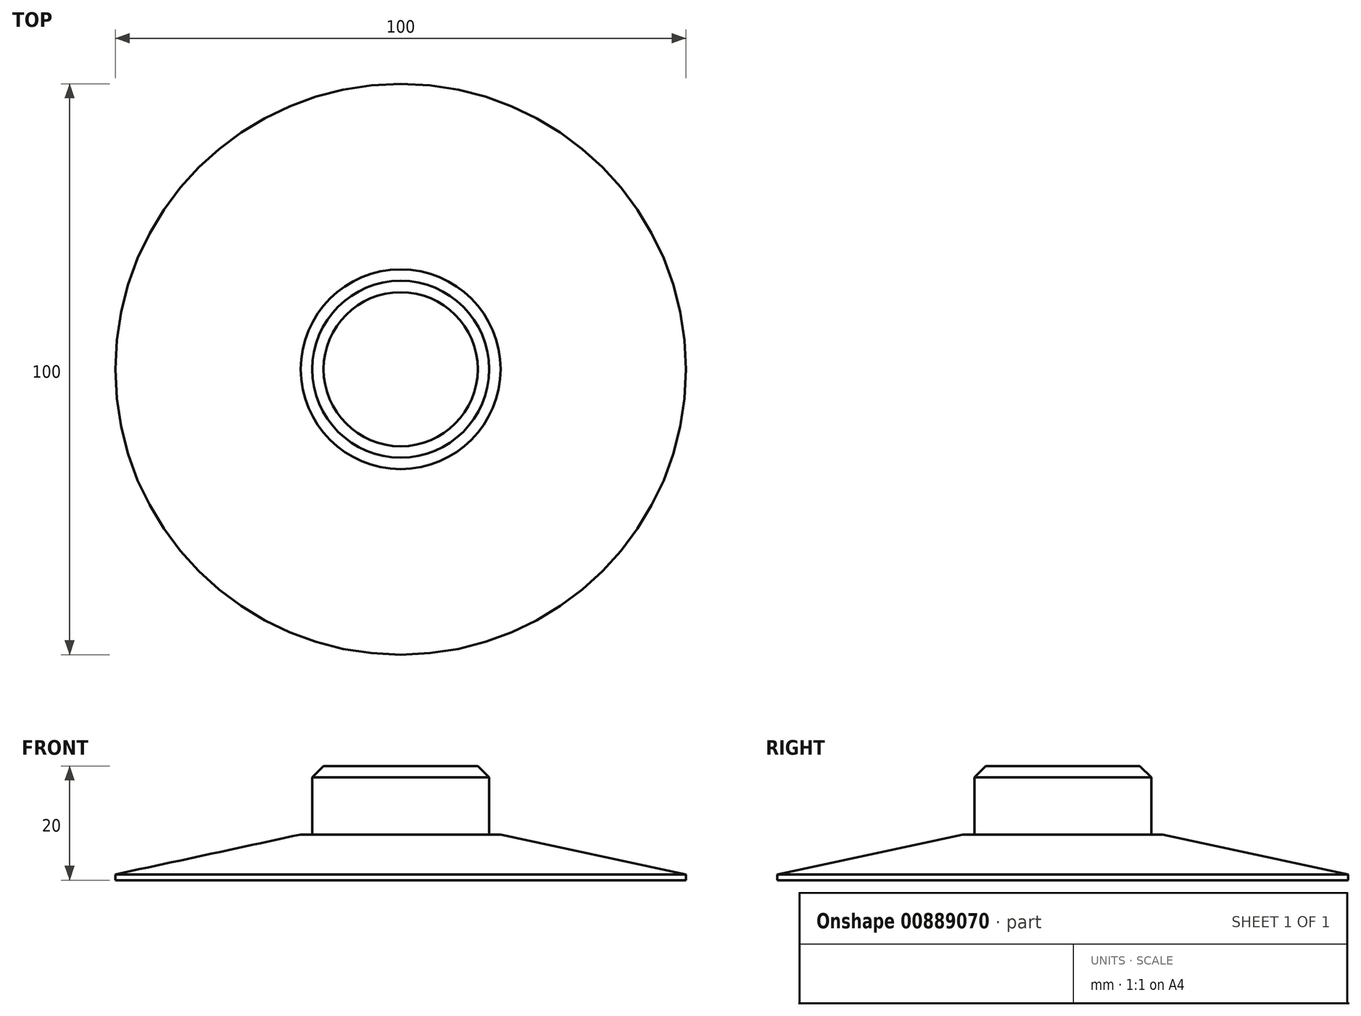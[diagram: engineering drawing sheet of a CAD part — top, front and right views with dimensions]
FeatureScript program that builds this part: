
annotation { "Feature Type Name" : "Feature", "Feature Type Description" : "" }
export const myFeature = defineFeature(function(context is Context, id is Id, definition is map)
    precondition{}
    {
        {
            var Q0;
            Q0=qCreatedBy(makeId("Front.planeOp"),FACE);
            var sketch = newSketch(context, id + "F0", { "sketchPlane" : qUnion([Q0])});
            skLineSegment(sketch, "E0", {"start": v(0, 0) * mm, "end": v(0, 20) * mm});
            skLineSegment(sketch, "E1", {"start": v(0, 20) * mm, "end": v(15.5, 20) * mm});
            skLineSegment(sketch, "E2", {"start": v(15.5, 20) * mm, "end": v(15.5, 8) * mm});
            skLineSegment(sketch, "E3", {"start": v(50, 1) * mm, "end": v(50, 0) * mm});
            skLineSegment(sketch, "E4", {"start": v(50, 0) * mm, "end": v(0, 0) * mm});
            skLineSegment(sketch, "E5", {"start": v(15.5, 8) * mm, "end": v(17.5, 8) * mm});
            skLineSegment(sketch, "E6", {"start": v(17.5, 8) * mm, "end": v(50, 1) * mm});
            skSolve(sketch);
        }
        {
            var Q0;
            Q0=makeQuery(id+"F0.imprint","IMPRINT",FACE,{"disambiguationData":[TD([[makeQuery(id+"F0.imprint","IMPRINT",EDGE,{"derivedFrom":sQuery(id+"F0.wireOp",EDGE,"E0")}),-1.0]])]});
            var Q1;
            Q1=sQuery(id+"F0.wireOp",EDGE,"E0");
            revolve(context, id + "F1", {"surfaceOperationType" : NewSurfaceOperationType.NEW, "entities" : qUnion([Q0]), "axis" : qUnion([Q1]), "revolveType" : RevolveType.FULL});
        }
        {
            var Q0;
            Q0=makeQuery(id+"F1.opRevolve","SWEPT_EDGE",EDGE,{"disambiguationData":[OSD([sQuery(id+"F0.wireOp",EDGE,"E1"),sQuery(id+"F0.wireOp",EDGE,"E2")])]});
            chamfer(context, id + "F2", {"entities" : qUnion([Q0]), "width" : 2 * mm, "tangentPropagation" : true});
        }
    });
